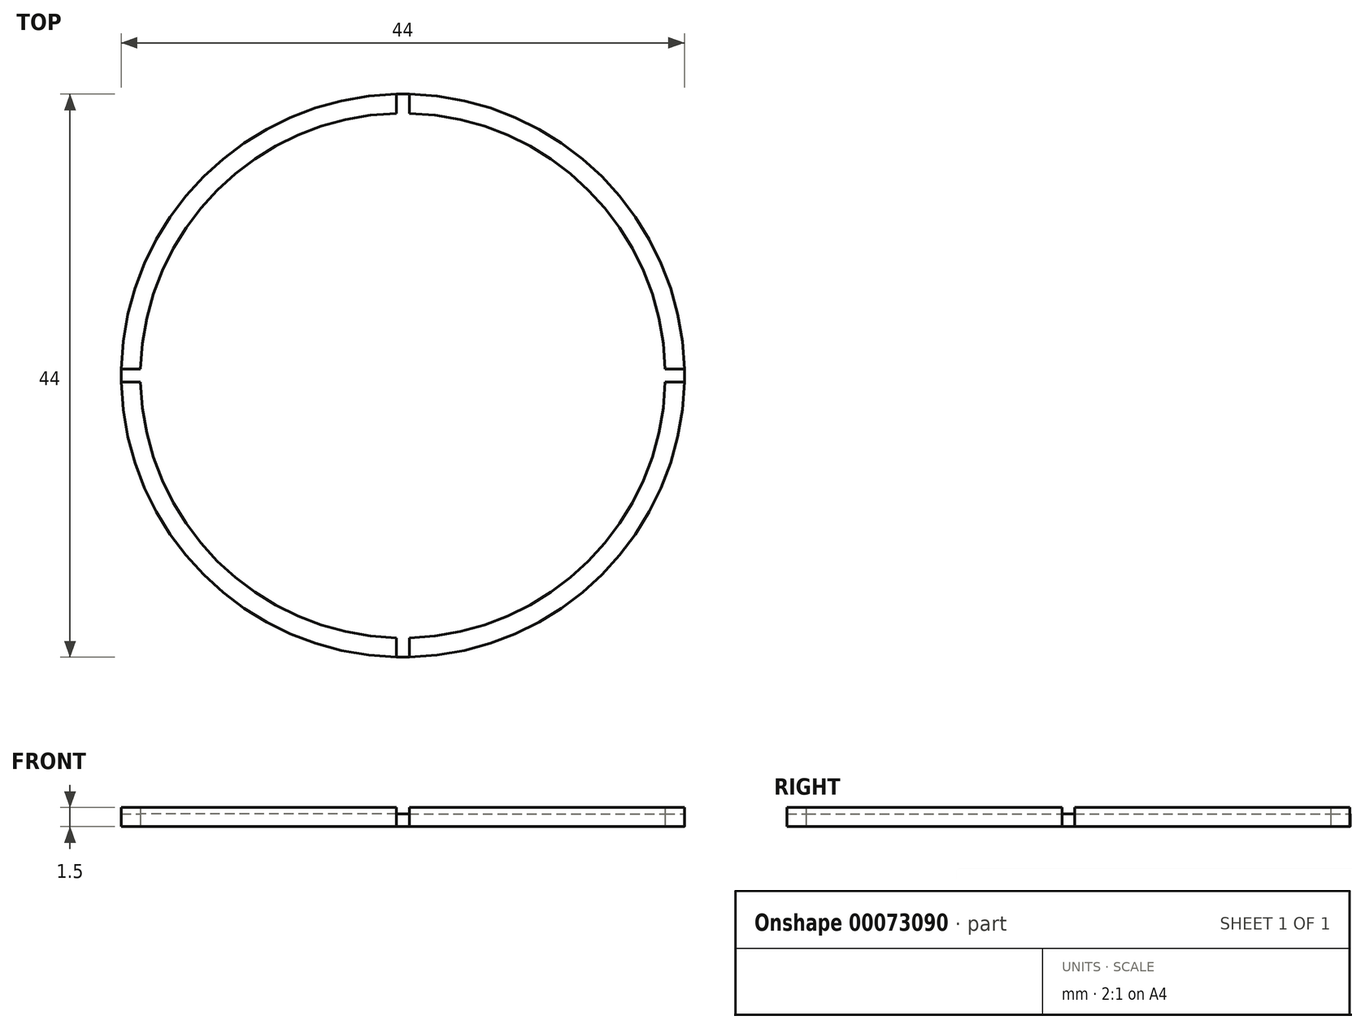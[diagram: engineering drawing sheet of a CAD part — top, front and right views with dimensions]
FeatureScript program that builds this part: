
annotation { "Feature Type Name" : "Feature", "Feature Type Description" : "" }
export const myFeature = defineFeature(function(context is Context, id is Id, definition is map)
    precondition{}
    {
        {
            var Q0;
            Q0=qCreatedBy(makeId("Top.planeOp"),FACE);
            var sketch = newSketch(context, id + "F0", { "sketchPlane" : qUnion([Q0])});
            skCircle(sketch, "E0", {"center": v(0, 0) * mm, "radius": 22 * mm});
            skCircle(sketch, "E1", {"center": v(0, 0) * mm, "radius": 20.5 * mm});
            skLineSegment(sketch, "E2", {"start": v(-22, 0.5) * mm, "end": v(-20.5, 0.5) * mm});
            skLineSegment(sketch, "E3", {"start": v(-22, -0.5) * mm, "end": v(-20.5, -0.5) * mm});
            skLineSegment(sketch, "E4", {"start": v(-0.5, 20.5) * mm, "end": v(-0.5, 22) * mm});
            skLineSegment(sketch, "E5", {"start": v(0.5, 20.5) * mm, "end": v(0.5, 22) * mm});
            skLineSegment(sketch, "E6", {"start": v(20.5, 0.5) * mm, "end": v(22, 0.5) * mm});
            skLineSegment(sketch, "E7", {"start": v(20.5, -0.5) * mm, "end": v(22, -0.5) * mm});
            skLineSegment(sketch, "E8", {"start": v(-0.5, -22) * mm, "end": v(-0.5, -20.5) * mm});
            skLineSegment(sketch, "E9", {"start": v(0.5, -22) * mm, "end": v(0.5, -20.5) * mm});
            skSolve(sketch);
        }
        {
            var Q0;
            {var subQ0=sQuery(id+"F0.wireOp",EDGE,"E2");Q0=makeQuery(id+"F0.imprint","IMPRINT",FACE,{"disambiguationData":[TD([[makeQuery(id+"F0.imprint","IMPRINT",EDGE,{"derivedFrom":subQ0}),1.0]])]});}
            var Q1;
            {var subQ0=sQuery(id+"F0.wireOp",EDGE,"E3");Q1=makeQuery(id+"F0.imprint","IMPRINT",FACE,{"disambiguationData":[TD([[makeQuery(id+"F0.imprint","IMPRINT",EDGE,{"derivedFrom":subQ0}),-1.0]])]});}
            var Q2;
            {var subQ0=sQuery(id+"F0.wireOp",EDGE,"E7");Q2=makeQuery(id+"F0.imprint","IMPRINT",FACE,{"disambiguationData":[TD([[makeQuery(id+"F0.imprint","IMPRINT",EDGE,{"derivedFrom":subQ0}),-1.0]])]});}
            var Q3;
            {var subQ0=sQuery(id+"F0.wireOp",EDGE,"E5");Q3=makeQuery(id+"F0.imprint","IMPRINT",FACE,{"disambiguationData":[TD([[makeQuery(id+"F0.imprint","IMPRINT",EDGE,{"derivedFrom":subQ0}),-1.0]])]});}
            extrude(context, id + "F1", {"entities" : qUnion([Q0, Q1, Q2, Q3]), "depth" : 1.5 * mm});
        }
        {
            var Q0;
            {var subQ0=sQuery(id+"F0.wireOp",EDGE,"E8");Q0=makeQuery(id+"F0.imprint","IMPRINT",FACE,{"disambiguationData":[TD([[makeQuery(id+"F0.imprint","IMPRINT",EDGE,{"derivedFrom":subQ0}),-1.0]])]});}
            var Q1;
            {var subQ0=sQuery(id+"F0.wireOp",EDGE,"E2");Q1=makeQuery(id+"F0.imprint","IMPRINT",FACE,{"disambiguationData":[TD([[makeQuery(id+"F0.imprint","IMPRINT",EDGE,{"derivedFrom":subQ0}),-1.0]])]});}
            var Q2;
            {var subQ0=sQuery(id+"F0.wireOp",EDGE,"E6");Q2=makeQuery(id+"F0.imprint","IMPRINT",FACE,{"disambiguationData":[TD([[makeQuery(id+"F0.imprint","IMPRINT",EDGE,{"derivedFrom":subQ0}),-1.0]])]});}
            var Q3;
            {var subQ0=sQuery(id+"F0.wireOp",EDGE,"E4");Q3=makeQuery(id+"F0.imprint","IMPRINT",FACE,{"disambiguationData":[TD([[makeQuery(id+"F0.imprint","IMPRINT",EDGE,{"derivedFrom":subQ0}),-1.0]])]});}
            var Q4;
            {var subQ0=sQuery(id+"F0.wireOp",EDGE,"E1");var subQ4=makeQuery(id+"F0.imprint","INTERSECT",VERTEX,{"derivedFrom":[subQ0,sQuery(id+"F0.wireOp",EDGE,"E5")]});Q4=makeQuery(id+"F0.imprint","IMPRINT",FACE,{"disambiguationData":[TD([[makeQuery(id+"F0.imprint","IMPRINT",EDGE,{"disambiguationData":[TD([[subQ4,1.0]])],"derivedFrom":subQ0}),1.0]])]});}
            extrude(context, id + "F2", {"entities" : qUnion([Q0, Q1, Q2, Q3, Q4]), "depth" : 1 * mm});
        }
    });
